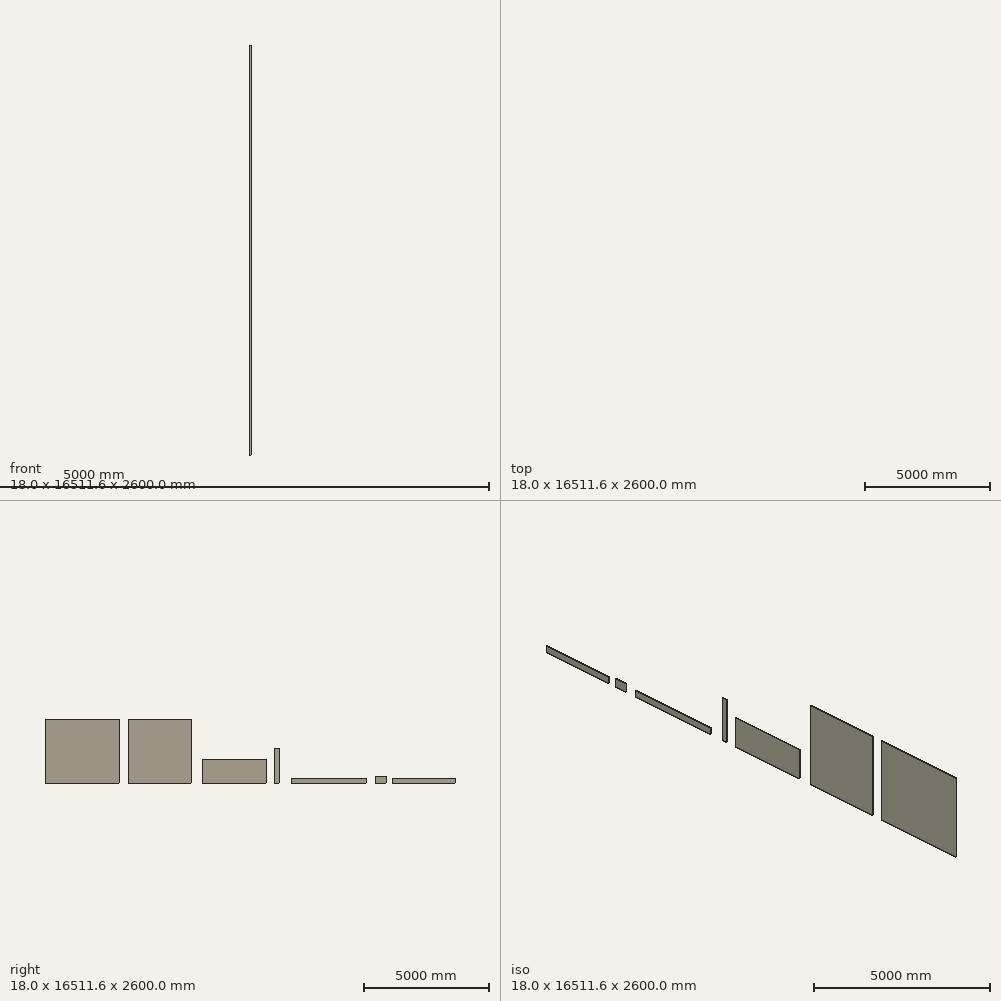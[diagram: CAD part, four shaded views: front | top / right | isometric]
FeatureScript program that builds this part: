
annotation { "Feature Type Name" : "Feature", "Feature Type Description" : "" }
export const myFeature = defineFeature(function(context is Context, id is Id, definition is map)
    precondition{}
    {
        {
            var Q0;
            Q0=qCreatedBy(makeId("Right.planeOp"),FACE);
            var sketch = newSketch(context, id + "F0", { "sketchPlane" : qUnion([Q0])});
            skLineSegment(sketch, "E0.bottom", {"start": v(0, 0) * mm, "end": v(2999.84, 0) * mm});
            skLineSegment(sketch, "E0.top", {"start": v(0, 2600) * mm, "end": v(2999.84, 2600) * mm});
            skLineSegment(sketch, "E0.left", {"start": v(0, 0) * mm, "end": v(0, 2600) * mm});
            skLineSegment(sketch, "E0.right", {"start": v(2999.84, 0) * mm, "end": v(2999.84, 2600) * mm});
            skSolve(sketch);
        }
        {
            var Q0;
            Q0=qSketchRegion(id+"F0",true);
            extrude(context, id + "F1", {"entities" : qUnion([Q0]), "depth" : 18 * mm, "offsetDistance" : 25 * mm});
        }
        {
            var Q0;
            Q0=qCreatedBy(makeId("Right.planeOp"),FACE);
            var sketch = newSketch(context, id + "F2", { "sketchPlane" : qUnion([Q0])});
            skLineSegment(sketch, "E1.bottom", {"start": v(3362.13, 0) * mm, "end": v(5882.13, 0) * mm});
            skLineSegment(sketch, "E1.top", {"start": v(3362.13, 2600) * mm, "end": v(5882.13, 2600) * mm});
            skLineSegment(sketch, "E1.left", {"start": v(3362.13, 0) * mm, "end": v(3362.13, 2600) * mm});
            skLineSegment(sketch, "E1.right", {"start": v(5882.13, 0) * mm, "end": v(5882.13, 2600) * mm});
            skSolve(sketch);
        }
        {
            var Q0;
            Q0=qSketchRegion(id+"F2",true);
            extrude(context, id + "F3", {"entities" : qUnion([Q0]), "depth" : 18 * mm, "offsetDistance" : 25 * mm});
        }
        {
            var Q0;
            Q0=qCreatedBy(makeId("Right.planeOp"),FACE);
            var sketch = newSketch(context, id + "F4", { "sketchPlane" : qUnion([Q0])});
            skLineSegment(sketch, "E2.bottom", {"start": v(6305.97, 0) * mm, "end": v(8885.97, 0) * mm});
            skLineSegment(sketch, "E2.top", {"start": v(6305.97, 965) * mm, "end": v(8885.97, 965) * mm});
            skLineSegment(sketch, "E2.left", {"start": v(6305.97, 0) * mm, "end": v(6305.97, 965) * mm});
            skLineSegment(sketch, "E2.right", {"start": v(8885.97, 0) * mm, "end": v(8885.97, 965) * mm});
            skSolve(sketch);
        }
        {
            var Q0;
            Q0=makeQuery(id+"F4.imprint","IMPRINT",FACE,{"disambiguationData":[TD([[makeQuery(id+"F4.imprint","IMPRINT",EDGE,{"derivedFrom":sQuery(id+"F4.wireOp",EDGE,"E2.bottom")}),1.0]])]});
            extrude(context, id + "F5", {"entities" : qUnion([Q0]), "depth" : 18 * mm, "offsetDistance" : 25 * mm});
        }
        {
            var Q0;
            Q0=qCreatedBy(makeId("Right.planeOp"),FACE);
            var sketch = newSketch(context, id + "F6", { "sketchPlane" : qUnion([Q0])});
            skLineSegment(sketch, "E3.bottom", {"start": v(9235.47, 0) * mm, "end": v(9425.47, 0) * mm});
            skLineSegment(sketch, "E3.top", {"start": v(9235.47, 1410) * mm, "end": v(9425.47, 1410) * mm});
            skLineSegment(sketch, "E3.left", {"start": v(9235.47, 0) * mm, "end": v(9235.47, 1410) * mm});
            skLineSegment(sketch, "E3.right", {"start": v(9425.47, 0) * mm, "end": v(9425.47, 1410) * mm});
            skSolve(sketch);
        }
        {
            var Q0;
            Q0=makeQuery(id+"F6.imprint","IMPRINT",FACE,{"disambiguationData":[TD([[makeQuery(id+"F6.imprint","IMPRINT",EDGE,{"derivedFrom":sQuery(id+"F6.wireOp",EDGE,"E3.bottom")}),1.0]])]});
            extrude(context, id + "F7", {"entities" : qUnion([Q0]), "depth" : 18 * mm, "offsetDistance" : 25 * mm});
        }
        {
            var Q0;
            Q0=qCreatedBy(makeId("Right.planeOp"),FACE);
            var sketch = newSketch(context, id + "F8", { "sketchPlane" : qUnion([Q0])});
            skLineSegment(sketch, "E4.bottom", {"start": v(9891.97, 0) * mm, "end": v(12909.97, 0) * mm});
            skLineSegment(sketch, "E4.top", {"start": v(9891.97, 220) * mm, "end": v(12909.97, 220) * mm});
            skLineSegment(sketch, "E4.left", {"start": v(9891.97, 0) * mm, "end": v(9891.97, 220) * mm});
            skLineSegment(sketch, "E4.right", {"start": v(12909.97, 0) * mm, "end": v(12909.97, 220) * mm});
            skSolve(sketch);
        }
        {
            var Q0;
            Q0=qSketchRegion(id+"F8",true);
            extrude(context, id + "F9", {"entities" : qUnion([Q0]), "depth" : 18 * mm, "offsetDistance" : 25 * mm});
        }
        {
            var Q0;
            Q0=qCreatedBy(makeId("Right.planeOp"),FACE);
            var sketch = newSketch(context, id + "F10", { "sketchPlane" : qUnion([Q0])});
            skLineSegment(sketch, "E5.bottom", {"start": v(13289.56, 0) * mm, "end": v(13729.56, 0) * mm});
            skLineSegment(sketch, "E5.top", {"start": v(13289.56, 283) * mm, "end": v(13729.56, 283) * mm});
            skLineSegment(sketch, "E5.left", {"start": v(13289.56, 0) * mm, "end": v(13289.56, 283) * mm});
            skLineSegment(sketch, "E5.right", {"start": v(13729.56, 0) * mm, "end": v(13729.56, 283) * mm});
            skSolve(sketch);
        }
        {
            var Q0;
            Q0=qSketchRegion(id+"F10",true);
            extrude(context, id + "F11", {"entities" : qUnion([Q0]), "depth" : 18 * mm, "offsetDistance" : 25 * mm});
        }
        {
            var Q0;
            Q0=qCreatedBy(makeId("Right.planeOp"),FACE);
            var sketch = newSketch(context, id + "F12", { "sketchPlane" : qUnion([Q0])});
            skLineSegment(sketch, "E6.bottom", {"start": v(13993.56, 0) * mm, "end": v(16511.56, 0) * mm});
            skLineSegment(sketch, "E6.top", {"start": v(13993.56, 220) * mm, "end": v(16511.56, 220) * mm});
            skLineSegment(sketch, "E6.left", {"start": v(13993.56, 0) * mm, "end": v(13993.56, 220) * mm});
            skLineSegment(sketch, "E6.right", {"start": v(16511.56, 0) * mm, "end": v(16511.56, 220) * mm});
            skSolve(sketch);
        }
        {
            var Q0;
            Q0=qSketchRegion(id+"F12",true);
            extrude(context, id + "F13", {"entities" : qUnion([Q0]), "depth" : 18 * mm, "offsetDistance" : 25 * mm});
        }
    });
